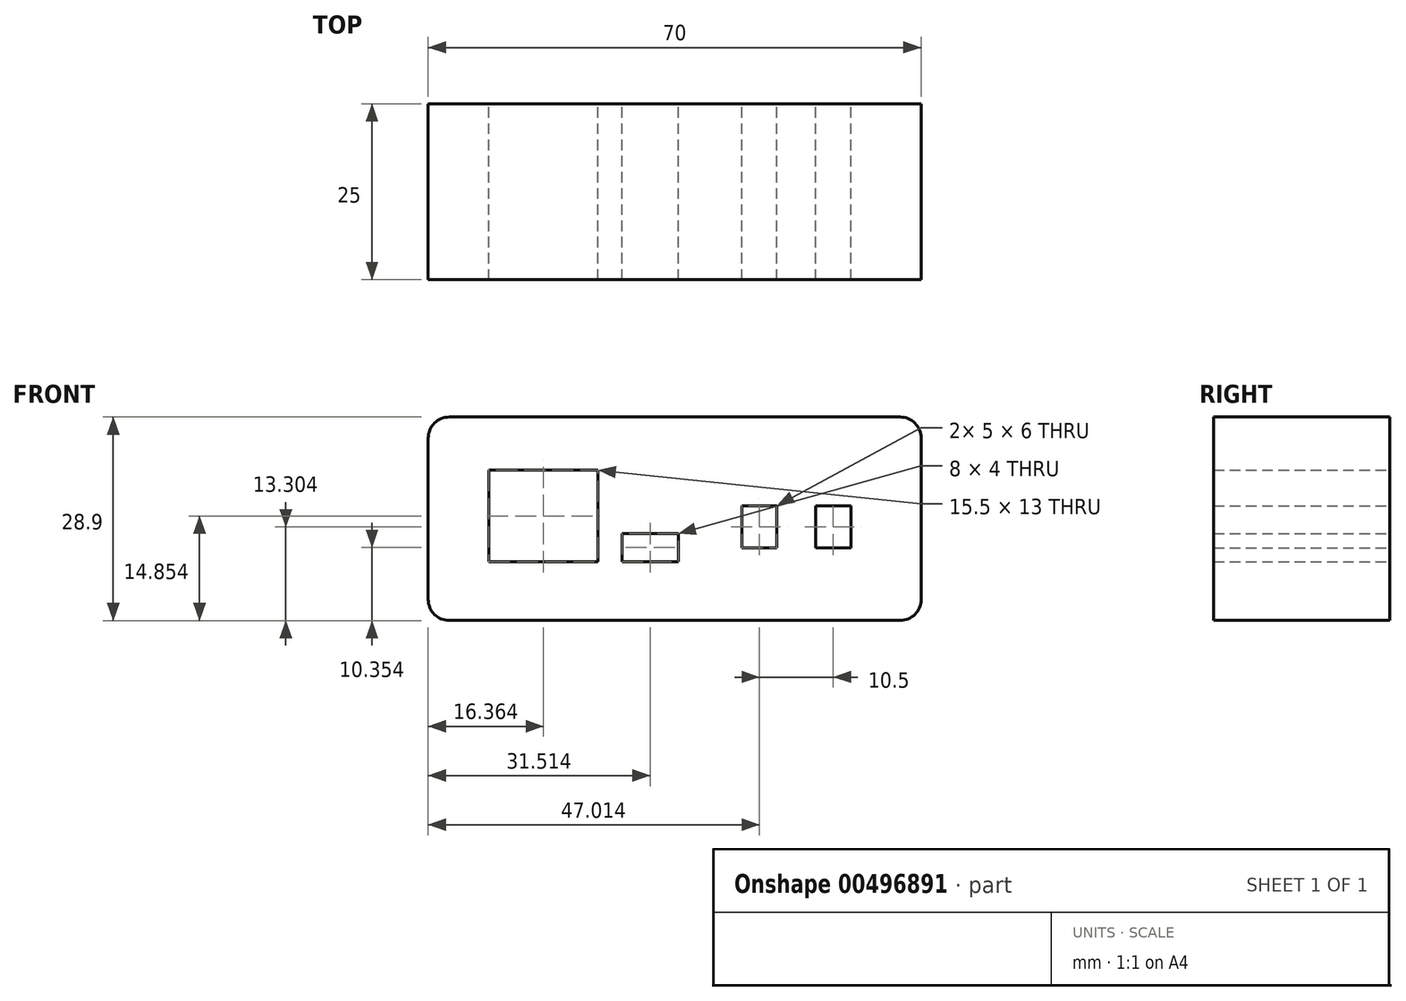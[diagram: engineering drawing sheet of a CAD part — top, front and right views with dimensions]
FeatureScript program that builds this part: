
annotation { "Feature Type Name" : "Feature", "Feature Type Description" : "" }
export const myFeature = defineFeature(function(context is Context, id is Id, definition is map)
    precondition{}
    {
        {
            var Q0;
            Q0=qCreatedBy(makeId("Front.planeOp"),FACE);
            var sketch = newSketch(context, id + "F0", { "sketchPlane" : qUnion([Q0])});
            skLineSegment(sketch, "E0.bottom", {"start": v(-29.21, 6.26) * mm, "end": v(34.79, 6.26) * mm});
            skLineSegment(sketch, "E0.top", {"start": v(-29.21, -22.64) * mm, "end": v(34.79, -22.64) * mm});
            skLineSegment(sketch, "E0.left", {"start": v(-32.21, 3.26) * mm, "end": v(-32.21, -19.64) * mm});
            skLineSegment(sketch, "E0.right", {"start": v(37.79, 3.26) * mm, "end": v(37.79, -19.64) * mm});
            skPoint(sketch, "E1.visualSharp", {"position": v(-32.21, 6.26) * mm});
            skArc(sketch, "E1.filletArc", {"start": v(-29.21, 6.26) * mm, "mid": v(-31.33, 5.39) * mm, "end": v(-32.21, 3.26) * mm});
            skPoint(sketch, "E2.visualSharp", {"position": v(-32.21, -22.64) * mm});
            skArc(sketch, "E2.filletArc", {"start": v(-32.21, -19.64) * mm, "mid": v(-31.33, -21.76) * mm, "end": v(-29.21, -22.64) * mm});
            skPoint(sketch, "E3.visualSharp", {"position": v(37.79, 6.26) * mm});
            skArc(sketch, "E3.filletArc", {"start": v(37.79, 3.26) * mm, "mid": v(36.9, 5.39) * mm, "end": v(34.79, 6.26) * mm});
            skPoint(sketch, "E4.visualSharp", {"position": v(37.79, -22.64) * mm});
            skArc(sketch, "E4.filletArc", {"start": v(34.79, -22.64) * mm, "mid": v(36.9, -21.76) * mm, "end": v(37.79, -19.64) * mm});
            skLineSegment(sketch, "E5.bottom", {"start": v(-23.6, -1.29) * mm, "end": v(-8.1, -1.29) * mm});
            skLineSegment(sketch, "E5.top", {"start": v(-23.6, -14.29) * mm, "end": v(-8.1, -14.29) * mm});
            skLineSegment(sketch, "E5.left", {"start": v(-23.6, -1.29) * mm, "end": v(-23.6, -14.29) * mm});
            skLineSegment(sketch, "E5.right", {"start": v(-8.1, -1.29) * mm, "end": v(-8.1, -14.29) * mm});
            skLineSegment(sketch, "E6.bottom", {"start": v(-4.7, -10.29) * mm, "end": v(3.3, -10.29) * mm});
            skLineSegment(sketch, "E6.top", {"start": v(-4.7, -14.29) * mm, "end": v(3.3, -14.29) * mm});
            skLineSegment(sketch, "E6.left", {"start": v(-4.7, -10.29) * mm, "end": v(-4.7, -14.29) * mm});
            skLineSegment(sketch, "E6.right", {"start": v(3.3, -10.29) * mm, "end": v(3.3, -14.29) * mm});
            skLineSegment(sketch, "E7.bottom", {"start": v(12.3, -6.34) * mm, "end": v(17.3, -6.34) * mm});
            skLineSegment(sketch, "E7.top", {"start": v(12.3, -12.34) * mm, "end": v(17.3, -12.34) * mm});
            skLineSegment(sketch, "E7.left", {"start": v(12.3, -6.34) * mm, "end": v(12.3, -12.34) * mm});
            skLineSegment(sketch, "E7.right", {"start": v(17.3, -6.34) * mm, "end": v(17.3, -12.34) * mm});
            skLineSegment(sketch, "E8.bottom", {"start": v(22.8, -6.34) * mm, "end": v(27.8, -6.34) * mm});
            skLineSegment(sketch, "E8.top", {"start": v(22.8, -12.34) * mm, "end": v(27.8, -12.34) * mm});
            skLineSegment(sketch, "E8.left", {"start": v(22.8, -6.34) * mm, "end": v(22.8, -12.34) * mm});
            skLineSegment(sketch, "E8.right", {"start": v(27.8, -6.34) * mm, "end": v(27.8, -12.34) * mm});
            skSolve(sketch);
        }
        {
            var Q0;
            Q0 = qSketchRegion(id + "F0", true);
            extrude(context, id + "F1", {"entities" : qUnion([Q0]), "depth" : 1.8 * mm});
        }
        {
            var Q0;
            Q0 = qSketchRegion(id + "F0", true);
            extrude(context, id + "F2", {"entities" : qUnion([Q0]), "operationType" : NewBodyOperationType.ADD, "depth" : 2 * mm});
        }
        {
            var Q0;
            Q0=makeQuery(id+"F2.opExtrude","CAP_FACE",FACE,{"disambiguationData":[OSD([sQuery(id+"F0.wireOp",EDGE,"E0.bottom"),sQuery(id+"F0.wireOp",EDGE,"E0.top"),sQuery(id+"F0.wireOp",EDGE,"E0.left"),sQuery(id+"F0.wireOp",EDGE,"E0.right"),sQuery(id+"F0.wireOp",EDGE,"E1.filletArc"),sQuery(id+"F0.wireOp",EDGE,"E2.filletArc"),sQuery(id+"F0.wireOp",EDGE,"E3.filletArc"),sQuery(id+"F0.wireOp",EDGE,"E4.filletArc"),sQuery(id+"F0.wireOp",EDGE,"E5.bottom"),sQuery(id+"F0.wireOp",EDGE,"E5.top"),sQuery(id+"F0.wireOp",EDGE,"E5.left"),sQuery(id+"F0.wireOp",EDGE,"E5.right"),sQuery(id+"F0.wireOp",EDGE,"E6.bottom"),sQuery(id+"F0.wireOp",EDGE,"E6.top"),sQuery(id+"F0.wireOp",EDGE,"E6.left"),sQuery(id+"F0.wireOp",EDGE,"E6.right"),sQuery(id+"F0.wireOp",EDGE,"E7.bottom"),sQuery(id+"F0.wireOp",EDGE,"E7.top"),sQuery(id+"F0.wireOp",EDGE,"E7.left"),sQuery(id+"F0.wireOp",EDGE,"E7.right"),sQuery(id+"F0.wireOp",EDGE,"E8.bottom"),sQuery(id+"F0.wireOp",EDGE,"E8.top"),sQuery(id+"F0.wireOp",EDGE,"E8.left"),sQuery(id+"F0.wireOp",EDGE,"E8.right")])],"isStart":false});
            extrude(context, id + "F3", {"entities" : qUnion([Q0]), "operationType" : NewBodyOperationType.ADD, "depth" : 2 * mm});
        }
        {
            var Q0;
            Q0 = qSketchRegion(id + "F0", true);
            extrude(context, id + "F4", {"entities" : qUnion([Q0]), "operationType" : NewBodyOperationType.ADD, "depth" : 25 * mm});
        }
        {
            var Q0;
            Q0 = qSketchRegion(id + "F0", true);
            extrude(context, id + "F5", {"entities" : qUnion([Q0]), "operationType" : NewBodyOperationType.ADD, "depth" : 25 * mm});
        }
    });
